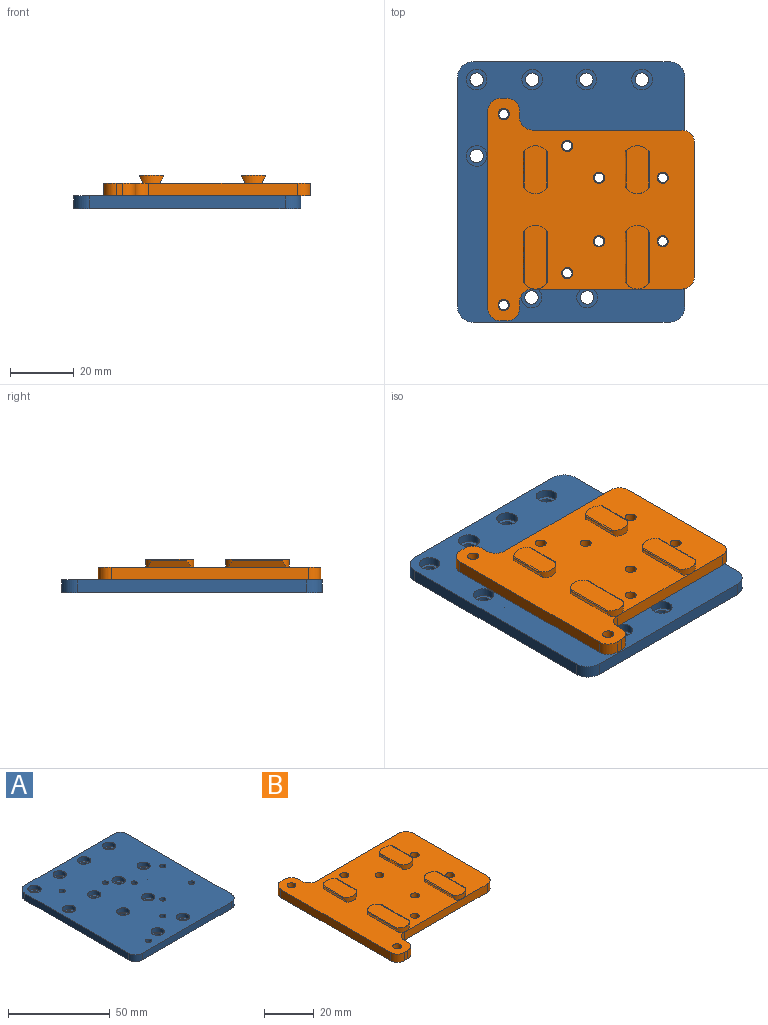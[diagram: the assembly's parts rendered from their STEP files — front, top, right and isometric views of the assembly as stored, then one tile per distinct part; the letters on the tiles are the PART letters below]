
ASSEMBLY  parts=2 mates=1
PART A: 122 faces, bbox 71.5x82x4 mm
  f0: plane 61.5x4mm, normal (0,-1,0), area 246mm2, adj f4,f5,f119,f120
  f1: plane 72x4mm, normal (1,0,0), area 288mm2, adj f4,f5,f120,f121
  f2: plane 61.5x4mm, normal (0,1,0), area 246mm2, adj f4,f5,f118,f121
  f3: plane 72x4mm, normal (-1,0,0), area 288mm2, adj f4,f5,f118,f119
  f4: plane 82x71.5mm, normal (0,0,-1), area 5396.4mm2, adj f0,f1,f2,f3,f6,f9,f12,f15
  f5: plane 82x71.5mm, normal (0,0,1), area 5386.8mm2, adj f0,f1,f2,f3,f8,f11,f14,f17
  f6: cylinder r=2.1mm len=4.2mm, axis (0,0,1), area 18.5mm2, adj f4,f7
  f7: plane 6.5x6.5mm, normal (0,0,1), area 19.3mm2, adj f6,f8
  f8: cylinder r=3.25mm len=6.5mm, axis (0,0,1), area 53.1mm2, adj f5,f7
  f9: cylinder r=2.1mm len=4.2mm, axis (0,0,1), area 18.5mm2, adj f4,f10
  f10: plane 6.5x6.5mm, normal (0,0,1), area 19.3mm2, adj f9,f11
  f11: cylinder r=3.25mm len=6.5mm, axis (0,0,1), area 53.1mm2, adj f5,f10
  f12: cylinder r=2.1mm len=4.2mm, axis (0,0,1), area 18.5mm2, adj f4,f13
  f13: plane 6.5x6.5mm, normal (0,0,1), area 19.3mm2, adj f12,f14
  f14: cylinder r=3.25mm len=6.5mm, axis (0,0,1), area 53.1mm2, adj f5,f13
  f15: cylinder r=2.1mm len=4.2mm, axis (0,0,1), area 18.5mm2, adj f4,f16
  f16: plane 6.5x6.5mm, normal (0,0,1), area 19.3mm2, adj f15,f17
  f17: cylinder r=3.25mm len=6.5mm, axis (0,0,1), area 53.1mm2, adj f5,f16
  f18: cylinder r=2.1mm len=4.2mm, axis (0,0,1), area 18.5mm2, adj f4,f19
  f19: plane 6.5x6.5mm, normal (0,0,1), area 19.3mm2, adj f18,f20
  f20: cylinder r=3.25mm len=6.5mm, axis (0,0,1), area 53.1mm2, adj f5,f19
  f21: cylinder r=2.1mm len=4.2mm, axis (0,0,1), area 18.5mm2, adj f4,f22
  f22: plane 6.5x6.5mm, normal (0,0,1), area 19.3mm2, adj f21,f23
  f23: cylinder r=3.25mm len=6.5mm, axis (0,0,1), area 53.1mm2, adj f5,f22
  f24: cylinder r=2.1mm len=4.2mm, axis (0,0,1), area 18.5mm2, adj f4,f25
  f25: plane 6.5x6.5mm, normal (0,0,1), area 19.3mm2, adj f24,f26
  f26: cylinder r=3.25mm len=6.5mm, axis (0,0,1), area 53.1mm2, adj f5,f25
  f27: cylinder r=2.1mm len=4.2mm, axis (0,0,1), area 18.5mm2, adj f4,f28
  f28: plane 6.5x6.5mm, normal (0,0,1), area 19.3mm2, adj f27,f29
  f29: cylinder r=3.25mm len=6.5mm, axis (0,0,1), area 53.1mm2, adj f5,f28
  f30: cylinder r=2.1mm len=4.2mm, axis (0,0,1), area 18.5mm2, adj f4,f31
  f31: plane 6.5x6.5mm, normal (0,0,1), area 19.3mm2, adj f30,f32
  f32: cylinder r=3.25mm len=6.5mm, axis (0,0,1), area 53.1mm2, adj f5,f31
  f33: cylinder r=2.1mm len=4.2mm, axis (0,0,1), area 18.5mm2, adj f4,f34
  f34: plane 6.5x6.5mm, normal (0,0,1), area 19.3mm2, adj f33,f35
  f35: cylinder r=3.25mm len=6.5mm, axis (0,0,1), area 53.1mm2, adj f5,f34
  f36: cylinder r=2.1mm len=4.2mm, axis (0,0,1), area 18.5mm2, adj f4,f37
  f37: plane 6.5x6.5mm, normal (0,0,1), area 19.3mm2, adj f36,f38
  f38: cylinder r=3.25mm len=6.5mm, axis (0,0,1), area 53.1mm2, adj f5,f37
  f39: cylinder r=2.1mm len=4.2mm, axis (0,0,1), area 18.5mm2, adj f4,f40
  f40: plane 6.5x6.5mm, normal (0,0,1), area 19.3mm2, adj f39,f41
  f41: cylinder r=3.25mm len=6.5mm, axis (0,0,1), area 53.1mm2, adj f5,f40
  f42: cone r=0mm half-angle=59deg, axis (0,0,-1), area 5.7mm2, adj f43
  f43: cylinder r=1.25mm len=3mm, axis (0,0,-1), area 23.6mm2, adj f4,f42
  f44: cone r=0mm half-angle=59deg, axis (0,0,-1), area 5.7mm2, adj f45
  f45: cylinder r=1.25mm len=3mm, axis (0,0,-1), area 23.6mm2, adj f4,f44
  f46: cone r=0mm half-angle=59deg, axis (0,0,-1), area 5.7mm2, adj f47
  f47: cylinder r=1.25mm len=3mm, axis (0,0,-1), area 23.6mm2, adj f4,f46
  f48: cone r=0mm half-angle=59deg, axis (0,0,-1), area 5.7mm2, adj f49
  f49: cylinder r=1.25mm len=3mm, axis (0,0,-1), area 23.6mm2, adj f4,f48
  f50: cone r=0mm half-angle=59deg, axis (0,0,-1), area 5.7mm2, adj f51
  f51: cylinder r=1.25mm len=3mm, axis (0,0,-1), area 23.6mm2, adj f4,f50
  f52: cone r=0mm half-angle=59deg, axis (0,0,-1), area 5.7mm2, adj f53
  f53: cylinder r=1.25mm len=3mm, axis (0,0,-1), area 23.6mm2, adj f4,f52
  f54: plane 3x2.2mm, normal (0.87,-0.5,0), area 7.6mm2, adj f4,f55,f59,f60
  f55: plane 3.46x2.2mm, normal (0,-1,0), area 7.6mm2, adj f4,f54,f56,f60
  f56: plane 3x2.2mm, normal (-0.87,-0.5,0), area 7.6mm2, adj f4,f55,f57,f60
  f57: plane 3x2.2mm, normal (-0.87,0.5,0), area 7.6mm2, adj f4,f56,f58,f60
  f58: plane 3.46x2.2mm, normal (0,1,0), area 7.6mm2, adj f4,f57,f59,f60
  f59: plane 3x2.2mm, normal (0.87,0.5,0), area 7.6mm2, adj f4,f54,f58,f60
  f60: plane 6.93x6mm, normal (0,0,-1), area 24.1mm2, adj f54,f55,f56,f57,f58,f59,f117
  f61: plane 3.46x2.2mm, normal (0,-1,0), area 7.6mm2, adj f4,f62,f66,f67
  f62: plane 3x2.2mm, normal (-0.87,-0.5,0), area 7.6mm2, adj f4,f61,f63,f67
  f63: plane 3x2.2mm, normal (-0.87,0.5,0), area 7.6mm2, adj f4,f62,f64,f67
  f64: plane 3.46x2.2mm, normal (0,1,0), area 7.6mm2, adj f4,f63,f65,f67
  f65: plane 3x2.2mm, normal (0.87,0.5,0), area 7.6mm2, adj f4,f64,f66,f67
  f66: plane 3x2.2mm, normal (0.87,-0.5,0), area 7.6mm2, adj f4,f61,f65,f67
  f67: plane 6.93x6mm, normal (0,0,-1), area 24.1mm2, adj f61,f62,f63,f64,f65,f66,f116
  f68: plane 3.46x2.2mm, normal (0,-1,0), area 7.6mm2, adj f4,f69,f73,f74
  f69: plane 3x2.2mm, normal (-0.87,-0.5,0), area 7.6mm2, adj f4,f68,f70,f74
  f70: plane 3x2.2mm, normal (-0.87,0.5,0), area 7.6mm2, adj f4,f69,f71,f74
  f71: plane 3.46x2.2mm, normal (0,1,0), area 7.6mm2, adj f4,f70,f72,f74
  f72: plane 3x2.2mm, normal (0.87,0.5,0), area 7.6mm2, adj f4,f71,f73,f74
  f73: plane 3x2.2mm, normal (0.87,-0.5,0), area 7.6mm2, adj f4,f68,f72,f74
  f74: plane 6.93x6mm, normal (0,0,-1), area 24.1mm2, adj f68,f69,f70,f71,f72,f73,f115
  f75: plane 3.46x2.2mm, normal (0,-1,0), area 7.6mm2, adj f4,f76,f80,f81
  f76: plane 3x2.2mm, normal (-0.87,-0.5,0), area 7.6mm2, adj f4,f75,f77,f81
  f77: plane 3x2.2mm, normal (-0.87,0.5,0), area 7.6mm2, adj f4,f76,f78,f81
  f78: plane 3.46x2.2mm, normal (0,1,0), area 7.6mm2, adj f4,f77,f79,f81
  f79: plane 3x2.2mm, normal (0.87,0.5,0), area 7.6mm2, adj f4,f78,f80,f81
  f80: plane 3x2.2mm, normal (0.87,-0.5,0), area 7.6mm2, adj f4,f75,f79,f81
  f81: plane 6.93x6mm, normal (0,0,-1), area 24.1mm2, adj f75,f76,f77,f78,f79,f80,f114
  f82: plane 3.46x2.2mm, normal (0,-1,0), area 7.6mm2, adj f4,f83,f87,f88
  f83: plane 3x2.2mm, normal (-0.87,-0.5,0), area 7.6mm2, adj f4,f82,f84,f88
  f84: plane 3x2.2mm, normal (-0.87,0.5,0), area 7.6mm2, adj f4,f83,f85,f88
  f85: plane 3.46x2.2mm, normal (0,1,0), area 7.6mm2, adj f4,f84,f86,f88
  f86: plane 3x2.2mm, normal (0.87,0.5,0), area 7.6mm2, adj f4,f85,f87,f88
  f87: plane 3x2.2mm, normal (0.87,-0.5,0), area 7.6mm2, adj f4,f82,f86,f88
  f88: plane 6.93x6mm, normal (0,0,-1), area 24.1mm2, adj f82,f83,f84,f85,f86,f87,f113
  f89: plane 3.46x2.2mm, normal (0,-1,0), area 7.6mm2, adj f4,f90,f94,f95
  f90: plane 3x2.2mm, normal (-0.87,-0.5,0), area 7.6mm2, adj f4,f89,f91,f95
  f91: plane 3x2.2mm, normal (-0.87,0.5,0), area 7.6mm2, adj f4,f90,f92,f95
  f92: plane 3.46x2.2mm, normal (0,1,0), area 7.6mm2, adj f4,f91,f93,f95
  f93: plane 3x2.2mm, normal (0.87,0.5,0), area 7.6mm2, adj f4,f92,f94,f95
  f94: plane 3x2.2mm, normal (0.87,-0.5,0), area 7.6mm2, adj f4,f89,f93,f95
  f95: plane 6.93x6mm, normal (0,0,-1), area 24.1mm2, adj f89,f90,f91,f92,f93,f94,f112
  f96: plane 3.46x2.2mm, normal (0,-1,0), area 7.6mm2, adj f4,f97,f101,f102
  f97: plane 3x2.2mm, normal (-0.87,-0.5,0), area 7.6mm2, adj f4,f96,f98,f102
  f98: plane 3x2.2mm, normal (-0.87,0.5,0), area 7.6mm2, adj f4,f97,f99,f102
  f99: plane 3.46x2.2mm, normal (0,1,0), area 7.6mm2, adj f4,f98,f100,f102
  f100: plane 3x2.2mm, normal (0.87,0.5,0), area 7.6mm2, adj f4,f99,f101,f102
  f101: plane 3x2.2mm, normal (0.87,-0.5,0), area 7.6mm2, adj f4,f96,f100,f102
  f102: plane 6.93x6mm, normal (0,0,-1), area 24.1mm2, adj f96,f97,f98,f99,f100,f101,f111
  f103: plane 3.46x2.2mm, normal (0,-1,0), area 7.6mm2, adj f4,f104,f108,f109
  f104: plane 3x2.2mm, normal (-0.87,-0.5,0), area 7.6mm2, adj f4,f103,f105,f109
  f105: plane 3x2.2mm, normal (-0.87,0.5,0), area 7.6mm2, adj f4,f104,f106,f109
  f106: plane 3.46x2.2mm, normal (0,1,0), area 7.6mm2, adj f4,f105,f107,f109
  f107: plane 3x2.2mm, normal (0.87,0.5,0), area 7.6mm2, adj f4,f106,f108,f109
  f108: plane 3x2.2mm, normal (0.87,-0.5,0), area 7.6mm2, adj f4,f103,f107,f109
  f109: plane 6.93x6mm, normal (0,0,-1), area 24.1mm2, adj f103,f104,f105,f106,f107,f108,f110
  f110: cylinder r=1.5mm len=3mm, axis (0,0,-1), area 17mm2, adj f5,f109
  f111: cylinder r=1.5mm len=3mm, axis (0,0,-1), area 17mm2, adj f5,f102
  f112: cylinder r=1.5mm len=3mm, axis (0,0,-1), area 17mm2, adj f5,f95
  f113: cylinder r=1.5mm len=3mm, axis (0,0,-1), area 17mm2, adj f5,f88
  f114: cylinder r=1.5mm len=3mm, axis (0,0,-1), area 17mm2, adj f5,f81
  f115: cylinder r=1.5mm len=3mm, axis (0,0,-1), area 17mm2, adj f5,f74
  f116: cylinder r=1.5mm len=3mm, axis (0,0,-1), area 17mm2, adj f5,f67
  f117: cylinder r=1.5mm len=3mm, axis (0,0,-1), area 17mm2, adj f5,f60
  f118: cylinder r=5mm len=5mm, axis (0,0,-1), area 31.4mm2, adj f2,f3,f4,f5
  f119: cylinder r=5mm len=5mm, axis (0,0,-1), area 31.4mm2, adj f0,f3,f4,f5
  f120: cylinder r=5mm len=5mm, axis (0,0,-1), area 31.4mm2, adj f0,f1,f4,f5
  f121: cylinder r=5mm len=5mm, axis (0,0,-1), area 31.4mm2, adj f1,f2,f4,f5
PART B: 54 faces, bbox 65.2x70.2x6.6 mm
  f0: plane 70x65mm, normal (0,0,1), area 3000.6mm2, adj f1,f2,f3,f4,f5,f6,f7,f8
  f1: plane 62x4mm, normal (-1,0,0), area 248mm2, adj f0,f9,f10,f17
  f2: plane 4x2.01mm, normal (0,-1,0), area 8mm2, adj f0,f9,f10,f11
  f3: plane 4x2mm, normal (1,0,0), area 8mm2, adj f0,f9,f11,f12
  f4: plane 46.99x4mm, normal (0,-1,0), area 188mm2, adj f0,f9,f12,f13
  f5: plane 42x4mm, normal (1,0,0), area 168mm2, adj f0,f9,f13,f14
  f6: plane 46.99x4mm, normal (0,1,0), area 188mm2, adj f0,f9,f14,f15
  f7: plane 4x2mm, normal (1,0,0), area 8mm2, adj f0,f9,f15,f16
  f8: plane 4x2.01mm, normal (0,1,0), area 8mm2, adj f0,f9,f16,f17
  f9: plane 70x65mm, normal (0,0,-1), area 3359.5mm2, adj f1,f2,f3,f4,f5,f6,f7,f8
  f10: cylinder r=4mm len=4mm, axis (0,0,-1), area 25.1mm2, adj f0,f1,f2,f9
  f11: cylinder r=4mm len=4mm, axis (0,0,-1), area 25.1mm2, adj f0,f2,f3,f9
  f12: cylinder r=4mm len=4mm, axis (0,0,1), area 25.1mm2, adj f0,f3,f4,f9
  f13: cylinder r=4mm len=4mm, axis (0,0,-1), area 25.1mm2, adj f0,f4,f5,f9
  f14: cylinder r=4mm len=4mm, axis (0,0,-1), area 25.1mm2, adj f0,f5,f6,f9
  f15: cylinder r=4mm len=4mm, axis (0,0,1), area 25.1mm2, adj f0,f6,f7,f9
  f16: cylinder r=4mm len=4mm, axis (0,0,-1), area 25.1mm2, adj f0,f7,f8,f9
  f17: cylinder r=4mm len=4mm, axis (0,0,-1), area 25.1mm2, adj f0,f1,f8,f9
  f18: cylinder r=1.75mm len=4mm, axis (0,0,-1), area 44mm2, adj f0,f9
  f19: cylinder r=1.75mm len=4mm, axis (0,0,-1), area 44mm2, adj f0,f9
  f20: cylinder r=1.75mm len=4mm, axis (0,0,-1), area 44mm2, adj f0,f9
  f21: cylinder r=1.75mm len=4mm, axis (0,0,-1), area 44mm2, adj f0,f9
  f22: cylinder r=1.75mm len=4mm, axis (0,0,-1), area 44mm2, adj f0,f9
  f23: cylinder r=1.75mm len=4mm, axis (0,0,-1), area 44mm2, adj f0,f9
  f24: cylinder r=1.75mm len=4mm, axis (0,0,-1), area 44mm2, adj f0,f9
  f25: cylinder r=1.75mm len=4mm, axis (0,0,-1), area 44mm2, adj f0,f9
  f26: cylinder r=4.78mm len=7.54mm, axis (0,0,-1), area 17.5mm2, adj f0,f27,f29,f30,f52,f53
  f27: plane 13.52x2.2mm, normal (-0.88,0,-0.47), area 27.7mm2, adj f0,f26,f28,f53
  f28: cylinder r=4.27mm len=7.55mm, axis (0,0,-1), area 18.3mm2, adj f0,f27,f29,f30,f52,f53
  f29: plane 13.52x2.2mm, normal (0.88,0,-0.47), area 27.7mm2, adj f0,f26,f28,f52
  f30: plane 15.02x6.89mm, normal (0,0,1), area 96.8mm2, adj f26,f28,f52,f53
  f31: plane 18.38x2.2mm, normal (0.88,0,-0.47), area 38.3mm2, adj f0,f32,f34,f47
  f32: cylinder r=4.27mm len=7.55mm, axis (0,0,-1), area 18.3mm2, adj f0,f31,f33,f35,f46,f47
  f33: plane 18.38x2.2mm, normal (-0.88,0,-0.47), area 38.3mm2, adj f0,f32,f34,f46
  f34: cylinder r=4.27mm len=7.55mm, axis (0,0,-1), area 18.3mm2, adj f0,f31,f33,f35,f46,f47
  f35: plane 20x6.89mm, normal (0,0,1), area 130.6mm2, adj f32,f34,f46,f47
  f36: plane 18.38x2.2mm, normal (-0.88,0,-0.47), area 38.3mm2, adj f0,f37,f39,f49
  f37: cylinder r=4.27mm len=7.55mm, axis (0,0,-1), area 18.3mm2, adj f0,f36,f38,f40,f48,f49
  f38: plane 18.38x2.2mm, normal (0.88,0,-0.47), area 38.3mm2, adj f0,f37,f39,f48
  f39: cylinder r=4.27mm len=7.55mm, axis (0,0,-1), area 18.3mm2, adj f0,f36,f38,f40,f48,f49
  f40: plane 20x6.89mm, normal (0,0,1), area 130.6mm2, adj f37,f39,f48,f49
  f41: cylinder r=4.78mm len=7.54mm, axis (0,0,-1), area 17.5mm2, adj f0,f42,f44,f45,f50,f51
  f42: plane 13.52x2.2mm, normal (-0.88,0,-0.47), area 27.7mm2, adj f0,f41,f43,f51
  f43: cylinder r=4.27mm len=7.55mm, axis (0,0,-1), area 18.3mm2, adj f0,f42,f44,f45,f50,f51
  f44: plane 13.52x2.2mm, normal (0.88,0,-0.47), area 27.7mm2, adj f0,f41,f43,f50
  f45: plane 15.02x6.89mm, normal (0,0,1), area 96.8mm2, adj f41,f43,f50,f51
  f46: bspline ~18.15x0.42mm, area 10.8mm2, adj f32,f33,f34,f35
  f47: bspline ~18.15x0.42mm, area 10.8mm2, adj f31,f32,f34,f35
  f48: bspline ~18.15x0.42mm, area 10.8mm2, adj f37,f38,f39,f40
  f49: bspline ~18.15x0.42mm, area 10.8mm2, adj f36,f37,f39,f40
  f50: bspline ~12.98x0.42mm, area 7.7mm2, adj f41,f43,f44,f45
  f51: bspline ~12.98x0.42mm, area 7.7mm2, adj f41,f42,f43,f45
  f52: bspline ~12.98x0.42mm, area 7.7mm2, adj f26,f28,f29,f30
  f53: bspline ~12.98x0.42mm, area 7.7mm2, adj f26,f27,f28,f30
PLACE A t=(32,-41,0)mm fixed
PLACE B t=(22.91,-55.97,0)mm
MATE fastened B.f23 <-> A.f111  axis (0,0,-1) through (14.51,-16.54,0)mm
